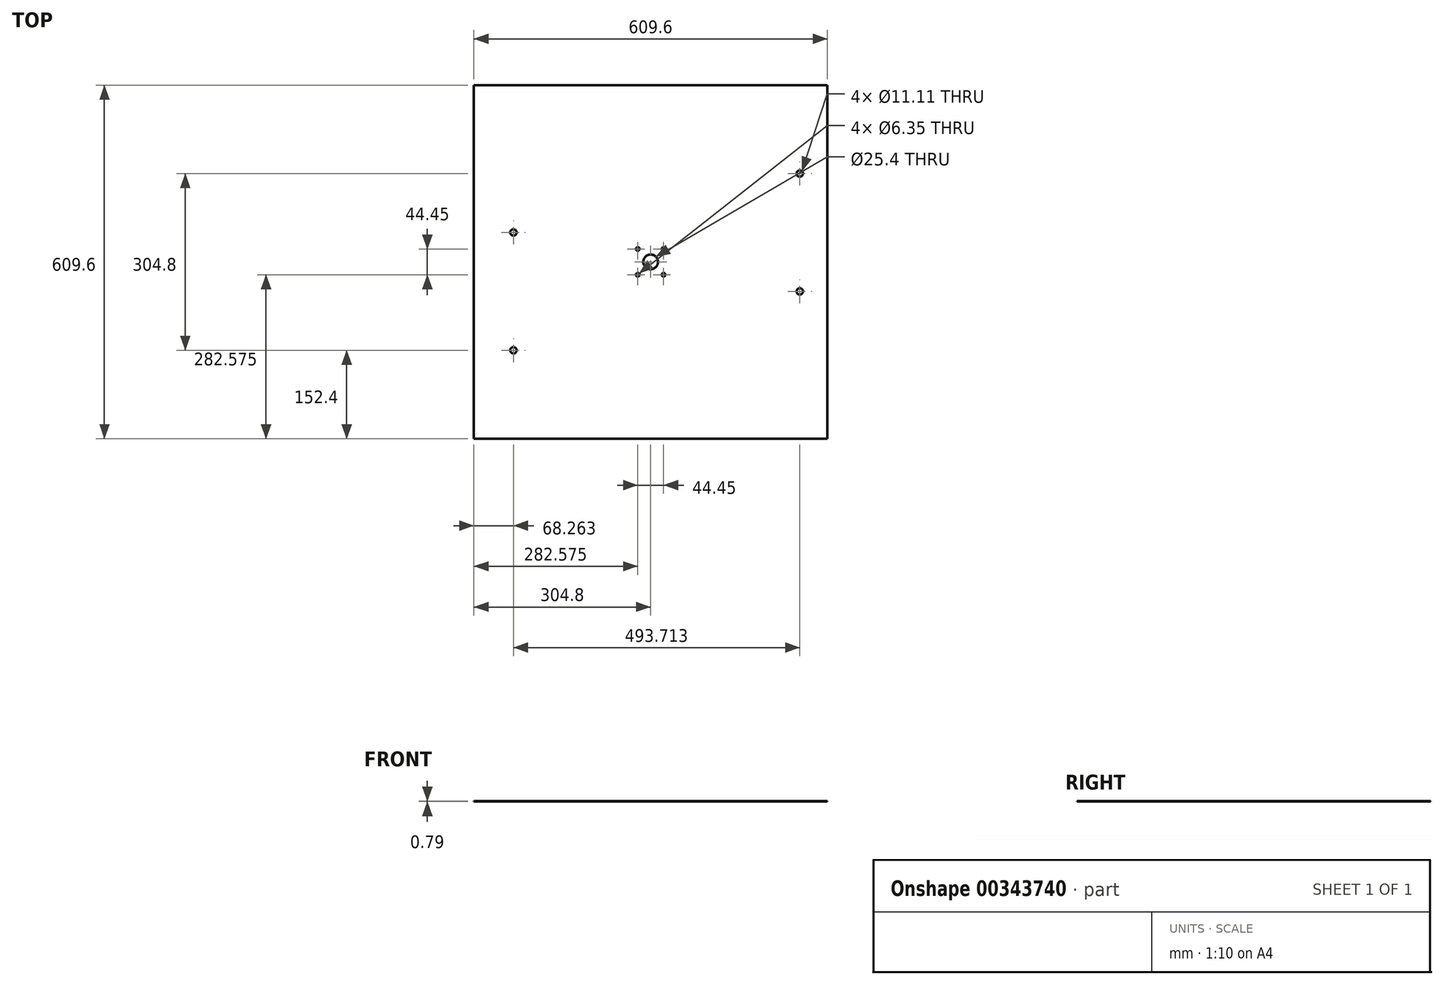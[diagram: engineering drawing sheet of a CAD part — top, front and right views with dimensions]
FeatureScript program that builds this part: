
annotation { "Feature Type Name" : "Feature", "Feature Type Description" : "" }
export const myFeature = defineFeature(function(context is Context, id is Id, definition is map)
    precondition{}
    {
        {
            var Q0;
            Q0=qCreatedBy(makeId("Top.planeOp"),FACE);
            var sketch = newSketch(context, id + "F0", { "sketchPlane" : qUnion([Q0])});
            skLineSegment(sketch, "E0.bottom", {"start": v(0, 0) * mm, "end": v(609.6, 0) * mm});
            skLineSegment(sketch, "E0.top", {"start": v(0, 609.6) * mm, "end": v(609.6, 609.6) * mm});
            skLineSegment(sketch, "E0.left", {"start": v(0, 0) * mm, "end": v(0, 609.6) * mm});
            skLineSegment(sketch, "E0.right", {"start": v(609.6, 0) * mm, "end": v(609.6, 609.6) * mm});
            skSolve(sketch);
        }
        {
            var Q0;
            Q0=makeQuery(id+"F0.imprint","IMPRINT",FACE,{"disambiguationData":[TD([[makeQuery(id+"F0.imprint","IMPRINT",EDGE,{"derivedFrom":sQuery(id+"F0.wireOp",EDGE,"E0.bottom")}),1.0]])]});
            extrude(context, id + "F1", {"entities" : qUnion([Q0]), "depth" : 0.8 * mm});
        }
        {
            var Q0;
            Q0=makeQuery(id+"F1.opExtrude","CAP_FACE",FACE,{"disambiguationData":[OSD([sQuery(id+"F0.wireOp",EDGE,"E0.bottom"),sQuery(id+"F0.wireOp",EDGE,"E0.top"),sQuery(id+"F0.wireOp",EDGE,"E0.left"),sQuery(id+"F0.wireOp",EDGE,"E0.right")])],"isStart":false});
            var sketch = newSketch(context, id + "F2", { "sketchPlane" : qUnion([Q0])});
            skCircle(sketch, "E1", {"center": v(68.26, 152.4) * mm, "radius": 5.56 * mm});
            skCircle(sketch, "E2", {"center": v(68.26, 355.6) * mm, "radius": 5.56 * mm});
            skCircle(sketch, "E3", {"center": v(561.98, 457.2) * mm, "radius": 5.56 * mm});
            skCircle(sketch, "E4", {"center": v(561.98, 254) * mm, "radius": 5.56 * mm});
            skSolve(sketch);
        }
        {
            var Q0;
            Q0=makeQuery(id+"F2.imprint","IMPRINT",FACE,{"disambiguationData":[TD([[makeQuery(id+"F2.imprint","IMPRINT",EDGE,{"derivedFrom":sQuery(id+"F2.wireOp",EDGE,"E1")}),1.0]])]});
            var Q1;
            Q1=makeQuery(id+"F2.imprint","IMPRINT",FACE,{"disambiguationData":[TD([[makeQuery(id+"F2.imprint","IMPRINT",EDGE,{"derivedFrom":sQuery(id+"F2.wireOp",EDGE,"E2")}),1.0]])]});
            var Q2;
            Q2=makeQuery(id+"F2.imprint","IMPRINT",FACE,{"disambiguationData":[TD([[makeQuery(id+"F2.imprint","IMPRINT",EDGE,{"derivedFrom":sQuery(id+"F2.wireOp",EDGE,"E4")}),1.0]])]});
            var Q3;
            Q3=makeQuery(id+"F2.imprint","IMPRINT",FACE,{"disambiguationData":[TD([[makeQuery(id+"F2.imprint","IMPRINT",EDGE,{"derivedFrom":sQuery(id+"F2.wireOp",EDGE,"E3")}),1.0]])]});
            extrude(context, id + "F3", {"entities" : qUnion([Q0, Q1, Q2, Q3]), "operationType" : NewBodyOperationType.REMOVE, "oppositeDirection" : true, "depth" : 25.4 * mm});
        }
        {
            var Q0;
            Q0=makeQuery(id+"F1.opExtrude","CAP_FACE",FACE,{"disambiguationData":[OSD([sQuery(id+"F0.wireOp",EDGE,"E0.bottom"),sQuery(id+"F0.wireOp",EDGE,"E0.top"),sQuery(id+"F0.wireOp",EDGE,"E0.left"),sQuery(id+"F0.wireOp",EDGE,"E0.right")])],"isStart":false});
            var sketch = newSketch(context, id + "F4", { "sketchPlane" : qUnion([Q0])});
            skLineSegment(sketch, "E5", {"start": v(304.8, 0) * mm, "end": v(304.8, 609.6) * mm, "construction": true});
            skLineSegment(sketch, "E6", {"start": v(0, 304.8) * mm, "end": v(609.6, 304.8) * mm, "construction": true});
            skCircle(sketch, "E7", {"center": v(304.8, 304.8) * mm, "radius": 12.7 * mm});
            skLineSegment(sketch, "E8.bottom", {"start": v(282.58, 327.03) * mm, "end": v(327.03, 327.03) * mm, "construction": true});
            skLineSegment(sketch, "E8.top", {"start": v(282.58, 282.58) * mm, "end": v(327.03, 282.58) * mm, "construction": true});
            skLineSegment(sketch, "E8.left", {"start": v(282.58, 327.03) * mm, "end": v(282.58, 282.58) * mm, "construction": true});
            skLineSegment(sketch, "E8.right", {"start": v(327.03, 327.03) * mm, "end": v(327.03, 282.58) * mm, "construction": true});
            skCircle(sketch, "E9", {"center": v(282.58, 282.58) * mm, "radius": 3.18 * mm});
            skCircle(sketch, "E10", {"center": v(327.03, 282.58) * mm, "radius": 3.18 * mm});
            skCircle(sketch, "E11", {"center": v(327.03, 327.03) * mm, "radius": 3.18 * mm});
            skCircle(sketch, "E12", {"center": v(282.58, 327.03) * mm, "radius": 3.18 * mm});
            skSolve(sketch);
        }
        {
            var Q0;
            Q0=makeQuery(id+"F4.imprint","IMPRINT",FACE,{"disambiguationData":[TD([[makeQuery(id+"F4.imprint","IMPRINT",EDGE,{"derivedFrom":sQuery(id+"F4.wireOp",EDGE,"E7")}),1.0]])]});
            var Q1;
            Q1=makeQuery(id+"F4.imprint","IMPRINT",FACE,{"disambiguationData":[TD([[makeQuery(id+"F4.imprint","IMPRINT",EDGE,{"derivedFrom":sQuery(id+"F4.wireOp",EDGE,"E12")}),1.0]])]});
            var Q2;
            Q2=makeQuery(id+"F4.imprint","IMPRINT",FACE,{"disambiguationData":[TD([[makeQuery(id+"F4.imprint","IMPRINT",EDGE,{"derivedFrom":sQuery(id+"F4.wireOp",EDGE,"E11")}),1.0]])]});
            var Q3;
            Q3=makeQuery(id+"F4.imprint","IMPRINT",FACE,{"disambiguationData":[TD([[makeQuery(id+"F4.imprint","IMPRINT",EDGE,{"derivedFrom":sQuery(id+"F4.wireOp",EDGE,"E10")}),1.0]])]});
            var Q4;
            Q4=makeQuery(id+"F4.imprint","IMPRINT",FACE,{"disambiguationData":[TD([[makeQuery(id+"F4.imprint","IMPRINT",EDGE,{"derivedFrom":sQuery(id+"F4.wireOp",EDGE,"E9")}),1.0]])]});
            extrude(context, id + "F5", {"entities" : qUnion([Q0, Q1, Q2, Q3, Q4]), "operationType" : NewBodyOperationType.REMOVE, "oppositeDirection" : true, "depth" : 25.4 * mm});
        }
    });
